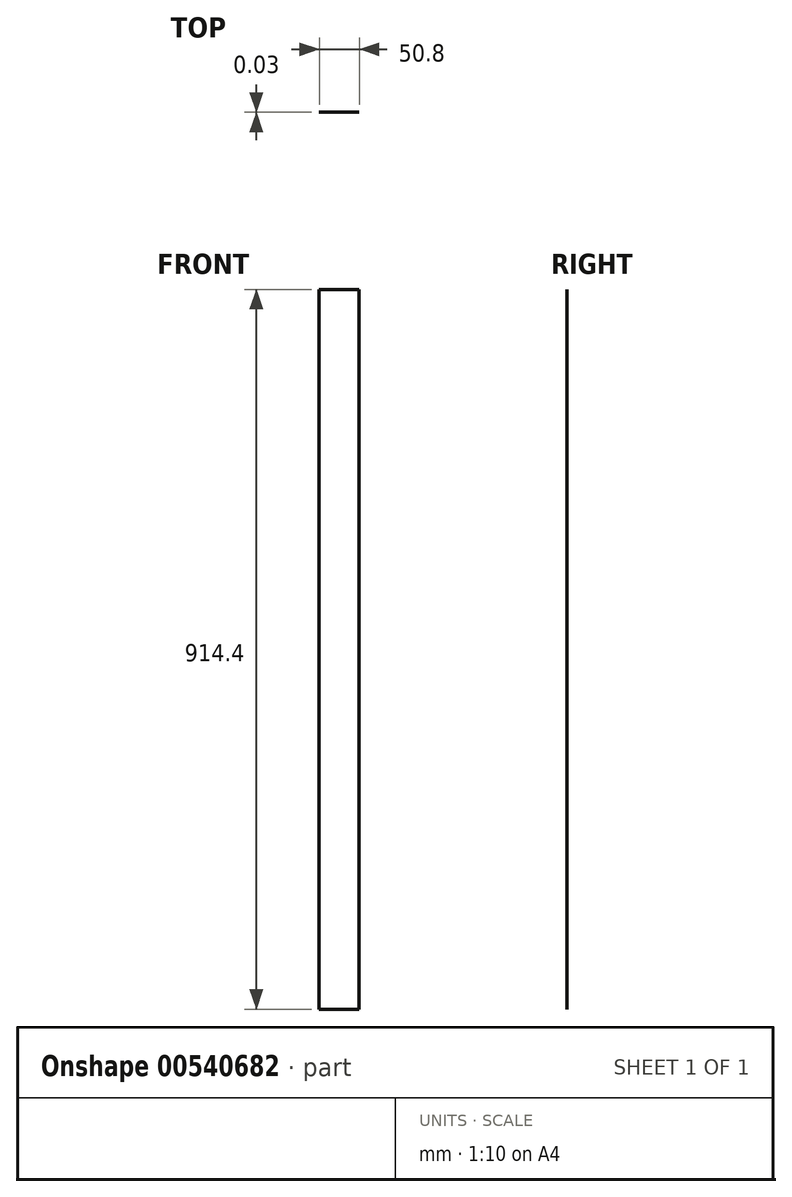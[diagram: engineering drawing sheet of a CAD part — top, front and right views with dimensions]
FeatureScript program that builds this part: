
annotation { "Feature Type Name" : "Feature", "Feature Type Description" : "" }
export const myFeature = defineFeature(function(context is Context, id is Id, definition is map)
    precondition{}
    {
        {
            var Q0;
            Q0=qCreatedBy(makeId("Front.planeOp"),FACE);
            var sketch = newSketch(context, id + "F0", { "sketchPlane" : qUnion([Q0])});
            skLineSegment(sketch, "E0", {"start": v(-54.7, -423.84) * mm, "end": v(-54.7, 490.56) * mm});
            skLineSegment(sketch, "E1", {"start": v(-54.7, -423.84) * mm, "end": v(-3.9, -423.84) * mm});
            skLineSegment(sketch, "E2", {"start": v(-3.9, -423.84) * mm, "end": v(-3.9, 490.56) * mm});
            skLineSegment(sketch, "E3", {"start": v(-54.7, 490.56) * mm, "end": v(-3.9, 490.56) * mm});
            skSolve(sketch);
        }
        {
            var Q0;
            Q0=makeQuery(id+"F0.imprint","IMPRINT",FACE,{"disambiguationData":[TD([[makeQuery(id+"F0.imprint","IMPRINT",EDGE,{"derivedFrom":sQuery(id+"F0.wireOp",EDGE,"E0")}),-1.0]])]});
            extrude(context, id + "F1", {"entities" : qUnion([Q0]), "depth" : 3 / 101.6 * mm, "offsetDistance" : 25.4 * mm});
        }
    });
